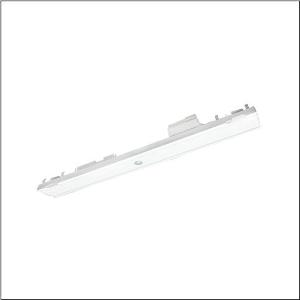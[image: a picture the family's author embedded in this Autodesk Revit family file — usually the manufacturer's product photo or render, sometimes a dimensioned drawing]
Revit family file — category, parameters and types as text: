
# Revit family: licross_r_56tl1e7c4x31_1f0a
name_source: partatom
category: Lighting Fixtures
units: mm (PartAtom-declared; Revit-internal decimal feet)

## family parameters
Cut with Voids When Loaded = No
Host = Face
Light Source = No
Part Type = Normal
Room Calculation Point = No
Round Connector Dimension = Use Diameter
Shared = No

## types (1)
- Licross® (1 x LED, 320 lm, 3.9 W, 4000K)
    Apparent Load = 4 VA
    CIE Flux Codes = 63 91 97 100 100
    Color Rendering = 70
    Color Temperature = 4000K
    Default Elevation = 1800 mm
    Description = Licross®, luminaire insert, of sheet steel, coil coated, white, length: 500mm, width: 59mm, height: 60mm, mounting height: 7..17m, emergency light element,LED rated luminous flux: 320lm, light colour: 740, control gear: CEAG, with plug, 6-pole, with phase selection, mains connection: 220..240V, AC/DC, 0/50..60Hz, rated input power: 3.9W, halogen-free wiring, for trunking rail, 9..14-pole, for emergency light function, supply monitoring module CEAG, with address switch, choice between two emergency light lines via tool-free moving of contact pin prior to installation in trunking rail, primary light control with lens, of PMMA, primary optical cover: cover, of PMMA, light emission: direct distribution, primary light characteristic: asymmetric,  for escape and rescue routes, compatible with all CEAG STAR technology systems (ZB-S, DG-S (DualGuard-S), LP-STAR, AT-S+), protection rating (complete): IP40, insulation class (complete): insulation class I (protective earthing), certification: CE, UKCA, protection symbol: D if used in an environment without relevant dust loads, impact resistance: IK06, permissible ambient temperature for indoor applications: -20..+40°C, packaging unit: 1 piece
    Height = 60 mm  [stored 0.19685 ft]
    Lamp = 1 x LED
    Lamp Light Flux = 320 lm
    Lamp Power = 3.9 W
    Lamp count = 1
    Length = 500 mm
    Luminous efficacy = 82 lm/W
    Manufacturer = Siteco
    ModVariant = No
    Model = 56TL1E7C4X31
    Mounting Place = Ceiling
    Mounting Type = Pendant
    Number of Poles = 1
    OnlyDefault = Yes
    Power Factor = 1
    Product Name = Licross®
    Product group = luminaire insert
    ProductGroupID = 901
    Protection Class = Protection class I
    Protection Degree = IP 40
    RLX_Detail_Level = 1
    RLX_Emergency_Light_Flux = 0 lm
    RLX_Emergency_Type = 0
    RLX_Emergency_Type_DB = No
    RlxData = <blob elided: 31229 chars, md5=1883f454>
    Socket = socket
    Standby Power = 0 W
    System Light Flux = 320 lm
    System Power = 4 W
    Type Comments = Product without accessories
    Type Image = l_1251804.jpg
    URL = http://relux.com
    VarID = ---
    Voltage = 0 V
    Weight = 0.00 kg
    Width = 59 mm

note: [stored X ft] marks values corroborated as IEEE doubles in the binary element streams (Revit-internal decimal feet)

## geometry (parser evidence)
native form markers: Blend x4, Sweep x12
no freeform markers — native parametric forms only
